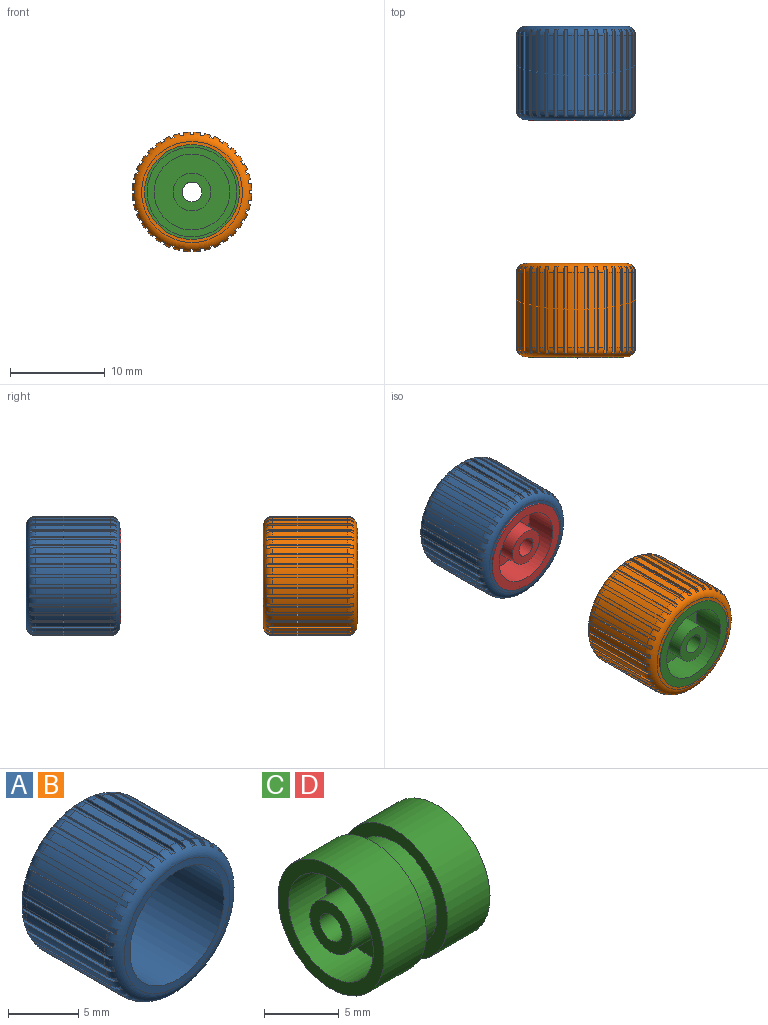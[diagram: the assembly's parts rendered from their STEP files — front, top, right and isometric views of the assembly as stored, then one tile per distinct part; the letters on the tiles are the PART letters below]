
ASSEMBLY  parts=4 mates=1
PART A: 149 faces, bbox 13.6x9.9x13.6 mm
  f0: cylinder r=6.3mm len=7.87mm, axis (0,1,0), area 5.6mm2, adj f39,f40,f41,f148
  f1: cylinder r=6.3mm len=7.87mm, axis (0,1,0), area 5.6mm2, adj f39,f40,f145,f146
  f2: cylinder r=6.3mm len=7.87mm, axis (0,1,0), area 5.6mm2, adj f39,f40,f142,f143
  f3: cylinder r=6.3mm len=7.87mm, axis (0,1,0), area 5.6mm2, adj f39,f40,f139,f140
  f4: cylinder r=6.3mm len=7.87mm, axis (0,1,0), area 5.6mm2, adj f39,f40,f136,f137
  f5: cylinder r=6.3mm len=7.87mm, axis (0,1,0), area 5.6mm2, adj f39,f40,f133,f134
  f6: cylinder r=6.3mm len=7.87mm, axis (0,1,0), area 5.6mm2, adj f39,f40,f130,f131
  f7: cylinder r=6.3mm len=7.87mm, axis (0,1,0), area 5.6mm2, adj f39,f40,f127,f128
  f8: cylinder r=6.3mm len=7.87mm, axis (0,1,0), area 5.6mm2, adj f39,f40,f124,f125
  f9: cylinder r=6.3mm len=7.87mm, axis (0,1,0), area 5.6mm2, adj f39,f40,f121,f122
  f10: cylinder r=6.3mm len=7.87mm, axis (0,1,0), area 5.6mm2, adj f39,f40,f118,f119
  f11: cylinder r=6.3mm len=7.87mm, axis (0,1,0), area 5.6mm2, adj f39,f40,f115,f116
  f12: cylinder r=6.3mm len=7.87mm, axis (0,1,0), area 5.6mm2, adj f39,f40,f112,f113
  f13: cylinder r=6.3mm len=7.87mm, axis (0,1,0), area 5.6mm2, adj f39,f40,f109,f110
  f14: cylinder r=6.3mm len=7.87mm, axis (0,1,0), area 5.6mm2, adj f39,f40,f106,f107
  f15: cylinder r=6.3mm len=7.87mm, axis (0,1,0), area 5.6mm2, adj f39,f40,f103,f104
  f16: cylinder r=6.3mm len=7.87mm, axis (0,1,0), area 5.6mm2, adj f39,f40,f100,f101
  f17: cylinder r=6.3mm len=7.87mm, axis (0,1,0), area 5.6mm2, adj f39,f40,f97,f98
  f18: cylinder r=6.3mm len=7.87mm, axis (0,1,0), area 5.6mm2, adj f39,f40,f94,f95
  f19: cylinder r=6.3mm len=7.87mm, axis (0,1,0), area 5.6mm2, adj f39,f40,f91,f92
  f20: cylinder r=6.3mm len=7.87mm, axis (0,1,0), area 5.6mm2, adj f39,f40,f88,f89
  f21: cylinder r=6.3mm len=7.87mm, axis (0,1,0), area 5.6mm2, adj f39,f40,f85,f86
  f22: cylinder r=6.3mm len=7.87mm, axis (0,1,0), area 5.6mm2, adj f39,f40,f82,f83
  f23: cylinder r=6.3mm len=7.87mm, axis (0,1,0), area 5.6mm2, adj f39,f40,f79,f80
  f24: cylinder r=6.3mm len=7.87mm, axis (0,1,0), area 5.6mm2, adj f39,f40,f76,f77
  f25: cylinder r=6.3mm len=7.87mm, axis (0,1,0), area 5.6mm2, adj f39,f40,f73,f74
  f26: cylinder r=6.3mm len=7.87mm, axis (0,1,0), area 5.6mm2, adj f39,f40,f70,f71
  f27: cylinder r=6.3mm len=7.87mm, axis (0,1,0), area 5.6mm2, adj f39,f40,f67,f68
  f28: cylinder r=6.3mm len=7.87mm, axis (0,1,0), area 5.6mm2, adj f39,f40,f64,f65
  f29: cylinder r=6.3mm len=7.87mm, axis (0,1,0), area 5.6mm2, adj f39,f40,f61,f62
  f30: cylinder r=6.3mm len=7.87mm, axis (0,1,0), area 5.6mm2, adj f39,f40,f58,f59
  f31: cylinder r=6.3mm len=7.87mm, axis (0,1,0), area 5.6mm2, adj f39,f40,f55,f56
  f32: cylinder r=6.3mm len=7.87mm, axis (0,1,0), area 5.6mm2, adj f39,f40,f52,f53
  f33: cylinder r=6.3mm len=7.87mm, axis (0,1,0), area 5.6mm2, adj f39,f40,f49,f50
  f34: cylinder r=6.3mm len=7.87mm, axis (0,1,0), area 5.6mm2, adj f39,f40,f46,f47
  f35: cylinder r=4.72mm len=9.84mm, axis (0,1,0), area 292.2mm2, adj f37,f38
  f36: cylinder r=6.3mm len=7.87mm, axis (0,1,0), area 5.6mm2, adj f39,f40,f43,f44
  f37: plane 10.63x10.63mm, normal (0,-1,0), area 18.6mm2, adj f35,f40
  f38: plane 10.63x10.63mm, normal (0,1,0), area 18.6mm2, adj f35,f39
  f39: torus R=5.31mm, axis (0,-1,0), area 47.8mm2, adj f0,f1,f2,f3,f4,f5,f6,f7
  f40: torus R=5.31mm, axis (0,-1,0), area 47.8mm2, adj f0,f1,f2,f3,f4,f5,f6,f7
  f41: plane 9.15x0.24mm, normal (1,0,0), area 2.1mm2, adj f0,f39,f40,f42
  f42: plane 9.17x0.4mm, normal (0,0,1), area 3.6mm2, adj f39,f40,f41,f43
  f43: plane 9.15x0.24mm, normal (-1,0,0), area 2.1mm2, adj f36,f39,f40,f42
  f44: plane 9.15x0.24mm, normal (0.98,0,-0.17), area 2.1mm2, adj f36,f39,f40,f45
  f45: plane 9.17x0.4mm, normal (0.17,0,0.98), area 3.6mm2, adj f39,f40,f44,f46
  f46: plane 9.15x0.24mm, normal (-0.98,0,0.17), area 2.1mm2, adj f34,f39,f40,f45
  f47: plane 9.15x0.22mm, normal (0.94,0,-0.34), area 2.1mm2, adj f34,f39,f40,f48
  f48: plane 9.17x0.38mm, normal (0.34,0,0.94), area 3.6mm2, adj f39,f40,f47,f49
  f49: plane 9.15x0.22mm, normal (-0.94,0,0.34), area 2.1mm2, adj f33,f39,f40,f48
  f50: plane 9.15x0.21mm, normal (0.87,0,-0.5), area 2.1mm2, adj f33,f39,f40,f51
  f51: plane 9.17x0.35mm, normal (0.5,0,0.87), area 3.6mm2, adj f39,f40,f50,f52
  f52: plane 9.15x0.21mm, normal (-0.87,0,0.5), area 2.1mm2, adj f32,f39,f40,f51
  f53: plane 9.15x0.18mm, normal (0.77,0,-0.64), area 2.1mm2, adj f32,f39,f40,f54
  f54: plane 9.17x0.31mm, normal (0.64,0,0.77), area 3.6mm2, adj f39,f40,f53,f55
  f55: plane 9.15x0.18mm, normal (-0.77,0,0.64), area 2.1mm2, adj f31,f39,f40,f54
  f56: plane 9.15x0.18mm, normal (0.64,0,-0.77), area 2.1mm2, adj f31,f39,f40,f57
  f57: plane 9.17x0.31mm, normal (0.77,0,0.64), area 3.6mm2, adj f39,f40,f56,f58
  f58: plane 9.15x0.18mm, normal (-0.64,0,0.77), area 2.1mm2, adj f30,f39,f40,f57
  f59: plane 9.15x0.21mm, normal (0.5,0,-0.87), area 2.1mm2, adj f30,f39,f40,f60
  f60: plane 9.17x0.35mm, normal (0.87,0,0.5), area 3.6mm2, adj f39,f40,f59,f61
  f61: plane 9.15x0.21mm, normal (-0.5,0,0.87), area 2.1mm2, adj f29,f39,f40,f60
  f62: plane 9.15x0.22mm, normal (0.34,0,-0.94), area 2.1mm2, adj f29,f39,f40,f63
  f63: plane 9.17x0.38mm, normal (0.94,0,0.34), area 3.6mm2, adj f39,f40,f62,f64
  f64: plane 9.15x0.22mm, normal (-0.34,0,0.94), area 2.1mm2, adj f28,f39,f40,f63
  f65: plane 9.15x0.24mm, normal (0.17,0,-0.98), area 2.1mm2, adj f28,f39,f40,f66
  f66: plane 9.17x0.4mm, normal (0.98,0,0.17), area 3.6mm2, adj f39,f40,f65,f67
  f67: plane 9.15x0.24mm, normal (-0.17,0,0.98), area 2.1mm2, adj f27,f39,f40,f66
  f68: plane 9.15x0.24mm, normal (0,0,-1), area 2.1mm2, adj f27,f39,f40,f69
  f69: plane 9.17x0.4mm, normal (1,0,0), area 3.6mm2, adj f39,f40,f68,f70
  f70: plane 9.15x0.24mm, normal (0,0,1), area 2.1mm2, adj f26,f39,f40,f69
  f71: plane 9.15x0.24mm, normal (-0.17,0,-0.98), area 2.1mm2, adj f26,f39,f40,f72
  f72: plane 9.17x0.4mm, normal (0.98,0,-0.17), area 3.6mm2, adj f39,f40,f71,f73
  f73: plane 9.15x0.24mm, normal (0.17,0,0.98), area 2.1mm2, adj f25,f39,f40,f72
  f74: plane 9.15x0.22mm, normal (-0.34,0,-0.94), area 2.1mm2, adj f25,f39,f40,f75
  f75: plane 9.17x0.38mm, normal (0.94,0,-0.34), area 3.6mm2, adj f39,f40,f74,f76
  f76: plane 9.15x0.22mm, normal (0.34,0,0.94), area 2.1mm2, adj f24,f39,f40,f75
  f77: plane 9.15x0.21mm, normal (-0.5,0,-0.87), area 2.1mm2, adj f24,f39,f40,f78
  f78: plane 9.17x0.35mm, normal (0.87,0,-0.5), area 3.6mm2, adj f39,f40,f77,f79
  f79: plane 9.15x0.21mm, normal (0.5,0,0.87), area 2.1mm2, adj f23,f39,f40,f78
  f80: plane 9.15x0.18mm, normal (-0.64,0,-0.77), area 2.1mm2, adj f23,f39,f40,f81
  f81: plane 9.17x0.31mm, normal (0.77,0,-0.64), area 3.6mm2, adj f39,f40,f80,f82
  f82: plane 9.15x0.18mm, normal (0.64,0,0.77), area 2.1mm2, adj f22,f39,f40,f81
  f83: plane 9.15x0.18mm, normal (-0.77,0,-0.64), area 2.1mm2, adj f22,f39,f40,f84
  f84: plane 9.17x0.31mm, normal (0.64,0,-0.77), area 3.6mm2, adj f39,f40,f83,f85
  f85: plane 9.15x0.18mm, normal (0.77,0,0.64), area 2.1mm2, adj f21,f39,f40,f84
  f86: plane 9.15x0.21mm, normal (-0.87,0,-0.5), area 2.1mm2, adj f21,f39,f40,f87
  f87: plane 9.17x0.35mm, normal (0.5,0,-0.87), area 3.6mm2, adj f39,f40,f86,f88
  f88: plane 9.15x0.21mm, normal (0.87,0,0.5), area 2.1mm2, adj f20,f39,f40,f87
  f89: plane 9.15x0.22mm, normal (-0.94,0,-0.34), area 2.1mm2, adj f20,f39,f40,f90
  f90: plane 9.17x0.38mm, normal (0.34,0,-0.94), area 3.6mm2, adj f39,f40,f89,f91
  f91: plane 9.15x0.22mm, normal (0.94,0,0.34), area 2.1mm2, adj f19,f39,f40,f90
  f92: plane 9.15x0.24mm, normal (-0.98,0,-0.17), area 2.1mm2, adj f19,f39,f40,f93
  f93: plane 9.17x0.4mm, normal (0.17,0,-0.98), area 3.6mm2, adj f39,f40,f92,f94
  f94: plane 9.15x0.24mm, normal (0.98,0,0.17), area 2.1mm2, adj f18,f39,f40,f93
  f95: plane 9.15x0.24mm, normal (-1,0,0), area 2.1mm2, adj f18,f39,f40,f96
  f96: plane 9.16x0.4mm, normal (0,0,-1), area 3.6mm2, adj f39,f40,f95,f97
  f97: plane 9.15x0.24mm, normal (1,0,0), area 2.1mm2, adj f17,f39,f40,f96
  f98: plane 9.15x0.24mm, normal (-0.98,0,0.17), area 2.1mm2, adj f17,f39,f40,f99
  f99: plane 9.17x0.4mm, normal (-0.17,0,-0.98), area 3.6mm2, adj f39,f40,f98,f100
  f100: plane 9.15x0.24mm, normal (0.98,0,-0.17), area 2.1mm2, adj f16,f39,f40,f99
  f101: plane 9.15x0.22mm, normal (-0.94,0,0.34), area 2.1mm2, adj f16,f39,f40,f102
  f102: plane 9.17x0.38mm, normal (-0.34,0,-0.94), area 3.6mm2, adj f39,f40,f101,f103
  f103: plane 9.15x0.22mm, normal (0.94,0,-0.34), area 2.1mm2, adj f15,f39,f40,f102
  f104: plane 9.15x0.21mm, normal (-0.87,0,0.5), area 2.1mm2, adj f15,f39,f40,f105
  f105: plane 9.17x0.35mm, normal (-0.5,0,-0.87), area 3.6mm2, adj f39,f40,f104,f106
  f106: plane 9.15x0.21mm, normal (0.87,0,-0.5), area 2.1mm2, adj f14,f39,f40,f105
  f107: plane 9.15x0.18mm, normal (-0.77,0,0.64), area 2.1mm2, adj f14,f39,f40,f108
  f108: plane 9.17x0.31mm, normal (-0.64,0,-0.77), area 3.6mm2, adj f39,f40,f107,f109
  f109: plane 9.15x0.18mm, normal (0.77,0,-0.64), area 2.1mm2, adj f13,f39,f40,f108
  f110: plane 9.15x0.18mm, normal (-0.64,0,0.77), area 2.1mm2, adj f13,f39,f40,f111
  f111: plane 9.17x0.31mm, normal (-0.77,0,-0.64), area 3.6mm2, adj f39,f40,f110,f112
  f112: plane 9.15x0.18mm, normal (0.64,0,-0.77), area 2.1mm2, adj f12,f39,f40,f111
  f113: plane 9.15x0.21mm, normal (-0.5,0,0.87), area 2.1mm2, adj f12,f39,f40,f114
  f114: plane 9.17x0.35mm, normal (-0.87,0,-0.5), area 3.6mm2, adj f39,f40,f113,f115
  f115: plane 9.15x0.21mm, normal (0.5,0,-0.87), area 2.1mm2, adj f11,f39,f40,f114
  f116: plane 9.15x0.22mm, normal (-0.34,0,0.94), area 2.1mm2, adj f11,f39,f40,f117
  f117: plane 9.17x0.38mm, normal (-0.94,0,-0.34), area 3.6mm2, adj f39,f40,f116,f118
  f118: plane 9.15x0.22mm, normal (0.34,0,-0.94), area 2.1mm2, adj f10,f39,f40,f117
  f119: plane 9.15x0.24mm, normal (-0.17,0,0.98), area 2.1mm2, adj f10,f39,f40,f120
  f120: plane 9.17x0.4mm, normal (-0.98,0,-0.17), area 3.6mm2, adj f39,f40,f119,f121
  f121: plane 9.15x0.24mm, normal (0.17,0,-0.98), area 2.1mm2, adj f9,f39,f40,f120
  f122: plane 9.15x0.24mm, normal (0,0,1), area 2.1mm2, adj f9,f39,f40,f123
  f123: plane 9.17x0.4mm, normal (-1,0,0), area 3.6mm2, adj f39,f40,f122,f124
  f124: plane 9.15x0.24mm, normal (0,0,-1), area 2.1mm2, adj f8,f39,f40,f123
  f125: plane 9.15x0.24mm, normal (0.17,0,0.98), area 2.1mm2, adj f8,f39,f40,f126
  f126: plane 9.17x0.4mm, normal (-0.98,0,0.17), area 3.6mm2, adj f39,f40,f125,f127
  f127: plane 9.15x0.24mm, normal (-0.17,0,-0.98), area 2.1mm2, adj f7,f39,f40,f126
  f128: plane 9.15x0.22mm, normal (0.34,0,0.94), area 2.1mm2, adj f7,f39,f40,f129
  f129: plane 9.17x0.38mm, normal (-0.94,0,0.34), area 3.6mm2, adj f39,f40,f128,f130
  f130: plane 9.15x0.22mm, normal (-0.34,0,-0.94), area 2.1mm2, adj f6,f39,f40,f129
  f131: plane 9.15x0.21mm, normal (0.5,0,0.87), area 2.1mm2, adj f6,f39,f40,f132
  f132: plane 9.17x0.35mm, normal (-0.87,0,0.5), area 3.6mm2, adj f39,f40,f131,f133
  f133: plane 9.15x0.21mm, normal (-0.5,0,-0.87), area 2.1mm2, adj f5,f39,f40,f132
  f134: plane 9.15x0.18mm, normal (0.64,0,0.77), area 2.1mm2, adj f5,f39,f40,f135
  f135: plane 9.17x0.31mm, normal (-0.77,0,0.64), area 3.6mm2, adj f39,f40,f134,f136
  f136: plane 9.15x0.18mm, normal (-0.64,0,-0.77), area 2.1mm2, adj f4,f39,f40,f135
  f137: plane 9.15x0.18mm, normal (0.77,0,0.64), area 2.1mm2, adj f4,f39,f40,f138
  f138: plane 9.17x0.31mm, normal (-0.64,0,0.77), area 3.6mm2, adj f39,f40,f137,f139
  f139: plane 9.15x0.18mm, normal (-0.77,0,-0.64), area 2.1mm2, adj f3,f39,f40,f138
  f140: plane 9.15x0.21mm, normal (0.87,0,0.5), area 2.1mm2, adj f3,f39,f40,f141
  f141: plane 9.17x0.35mm, normal (-0.5,0,0.87), area 3.6mm2, adj f39,f40,f140,f142
  f142: plane 9.15x0.21mm, normal (-0.87,0,-0.5), area 2.1mm2, adj f2,f39,f40,f141
  f143: plane 9.15x0.22mm, normal (0.94,0,0.34), area 2.1mm2, adj f2,f39,f40,f144
  f144: plane 9.17x0.38mm, normal (-0.34,0,0.94), area 3.6mm2, adj f39,f40,f143,f145
  f145: plane 9.15x0.22mm, normal (-0.94,0,-0.34), area 2.1mm2, adj f1,f39,f40,f144
  f146: plane 9.15x0.24mm, normal (0.98,0,0.17), area 2.1mm2, adj f1,f39,f40,f147
  f147: plane 9.17x0.4mm, normal (-0.17,0,0.98), area 3.6mm2, adj f39,f40,f146,f148
  f148: plane 9.15x0.24mm, normal (-0.98,0,-0.17), area 2.1mm2, adj f0,f39,f40,f147
PART B: same geometry as A
PART C: 30 faces, bbox 10x10x10 mm
  f0: plane 3.74x3.74mm, normal (1,0,0), area 8.4mm2, adj f4,f25,f26,f27
  f1: plane 3.74x3.74mm, normal (1,0,0), area 8.4mm2, adj f4,f22,f23,f24
  f2: plane 3.74x3.74mm, normal (1,0,0), area 8.4mm2, adj f4,f19,f20,f21
  f3: plane 3.74x3.74mm, normal (1,0,0), area 8.4mm2, adj f4,f16,f17,f18
  f4: cylinder r=4mm len=8mm, axis (1,0,0), area 86.4mm2, adj f0,f1,f2,f3,f5,f16,f18,f19
  f5: plane 10x10mm, normal (1,0,0), area 28.3mm2, adj f4,f6
  f6: cylinder r=5mm len=10mm, axis (1,0,0), area 125.7mm2, adj f5,f7
  f7: plane 10x10mm, normal (-1,0,0), area 28.3mm2, adj f6,f8
  f8: cylinder r=4mm len=8mm, axis (1,0,0), area 50.3mm2, adj f7,f9
  f9: plane 10x10mm, normal (1,0,0), area 28.3mm2, adj f8,f10
  f10: cylinder r=5mm len=10mm, axis (1,0,0), area 125.7mm2, adj f9,f11
  f11: plane 10x10mm, normal (-1,0,0), area 28.3mm2, adj f10,f12
  f12: cylinder r=4mm len=8mm, axis (1,0,0), area 88mm2, adj f11,f13
  f13: plane 8x8mm, normal (-1,0,0), area 37.7mm2, adj f12,f14
  f14: cylinder r=2mm len=4mm, axis (1,0,0), area 44mm2, adj f13,f15
  f15: plane 4x4mm, normal (-1,0,0), area 9.1mm2, adj f14,f29
  f16: plane 2.01x0.8mm, normal (0,-1,0), area 1.6mm2, adj f3,f4,f17,f28
  f17: cylinder r=2mm len=1.73mm, axis (-1,0,0), area 2.1mm2, adj f3,f16,f18,f28
  f18: plane 2.01x0.8mm, normal (0,0,1), area 1.6mm2, adj f3,f4,f17,f28
  f19: plane 2.01x0.8mm, normal (0,0,-1), area 1.6mm2, adj f2,f4,f20,f28
  f20: cylinder r=2mm len=1.73mm, axis (-1,0,0), area 2.1mm2, adj f2,f19,f21,f28
  f21: plane 2.01x0.8mm, normal (0,-1,0), area 1.6mm2, adj f2,f4,f20,f28
  f22: plane 2.01x0.8mm, normal (0,1,0), area 1.6mm2, adj f1,f4,f23,f28
  f23: cylinder r=2mm len=1.73mm, axis (-1,0,0), area 2.1mm2, adj f1,f22,f24,f28
  f24: plane 2.01x0.8mm, normal (0,0,-1), area 1.6mm2, adj f1,f4,f23,f28
  f25: plane 2.01x0.8mm, normal (0,0,1), area 1.6mm2, adj f0,f4,f26,f28
  f26: cylinder r=2mm len=1.73mm, axis (-1,0,0), area 2.1mm2, adj f0,f25,f27,f28
  f27: plane 2.01x0.8mm, normal (0,1,0), area 1.6mm2, adj f0,f4,f26,f28
  f28: plane 8x8mm, normal (1,0,0), area 13.1mm2, adj f4,f16,f17,f18,f19,f20,f21,f22
  f29: cylinder r=1.05mm len=7.3mm, axis (-1,0,0), area 48mm2, adj f15,f28
PART D: same geometry as C
PLACE A t=(-6.75,25.29,1.79)mm
PLACE B t=(-6.75,0.29,1.79)mm
PLACE C rot(axis=(0.58,0.58,0.58),120deg) t=(-6.75,-4.67,1.79)mm
PLACE D rot(axis=(0.58,0.58,0.58),120deg) t=(-6.75,20.33,1.79)mm
MATE slider B.f0 <-> C.f4  axis (0,1,0) through (-6.75,-4.63,1.79)mm
